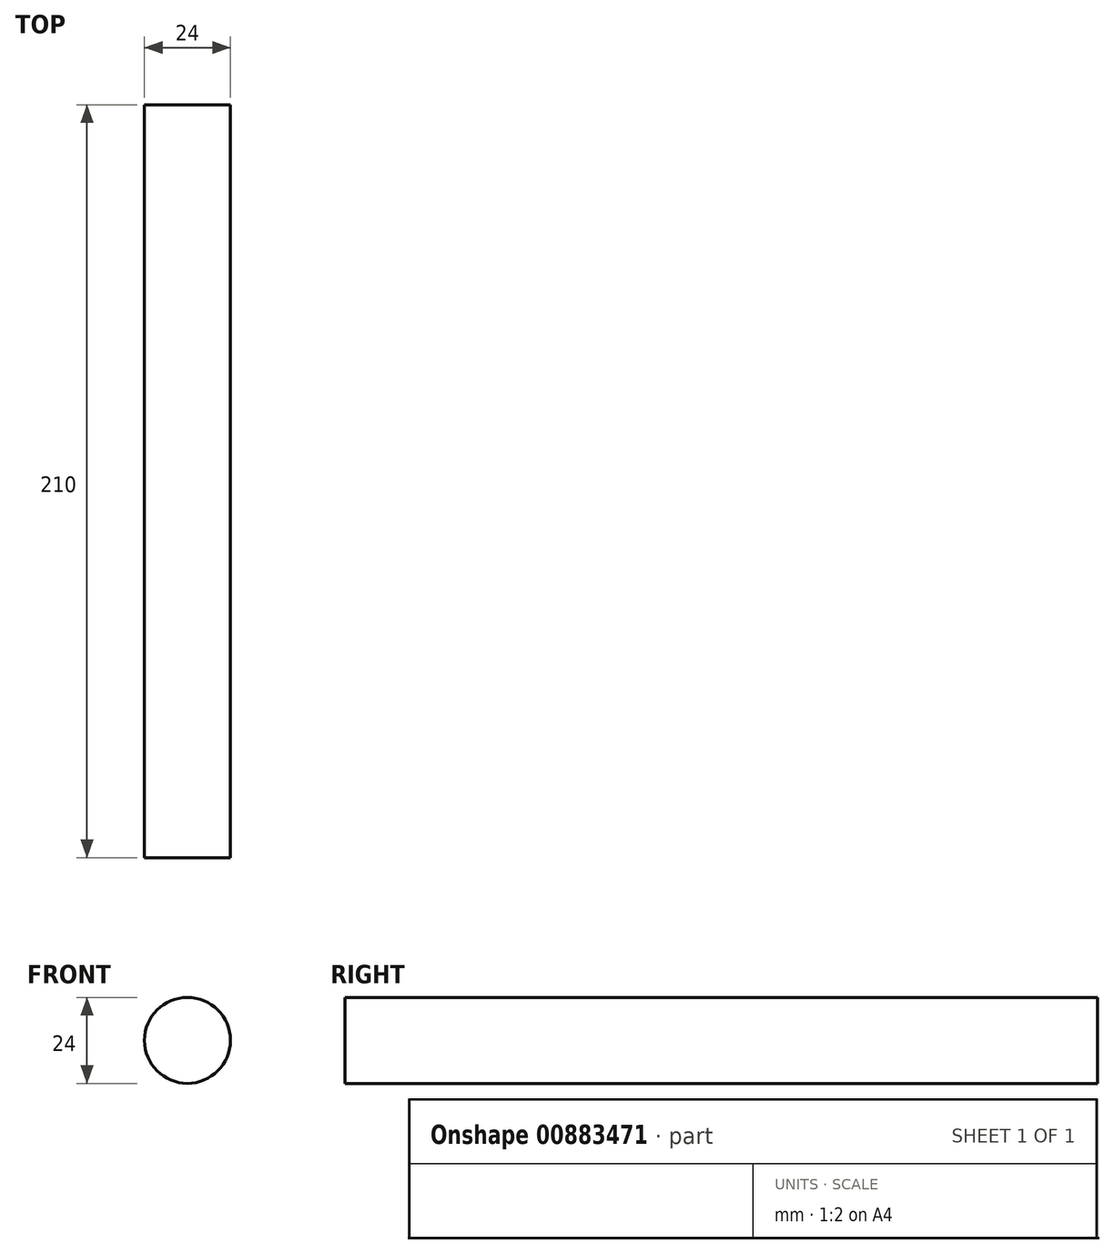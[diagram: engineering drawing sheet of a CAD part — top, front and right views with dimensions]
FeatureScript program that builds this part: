
annotation { "Feature Type Name" : "Feature", "Feature Type Description" : "" }
export const myFeature = defineFeature(function(context is Context, id is Id, definition is map)
    precondition{}
    {
        {
            var Q0;
            Q0=qCreatedBy(makeId("Front.planeOp"),FACE);
            var sketch = newSketch(context, id + "F0", { "sketchPlane" : qUnion([Q0])});
            skCircle(sketch, "E0", {"center": v(0, 0) * mm, "radius": 12 * mm});
            skSolve(sketch);
        }
        {
            var Q0;
            Q0 = qSketchRegion(id + "F0", true);
            extrude(context, id + "F1", {"entities" : qUnion([Q0]), "depth" : 210 * mm, "offsetDistance" : 25 * mm});
        }
    });
